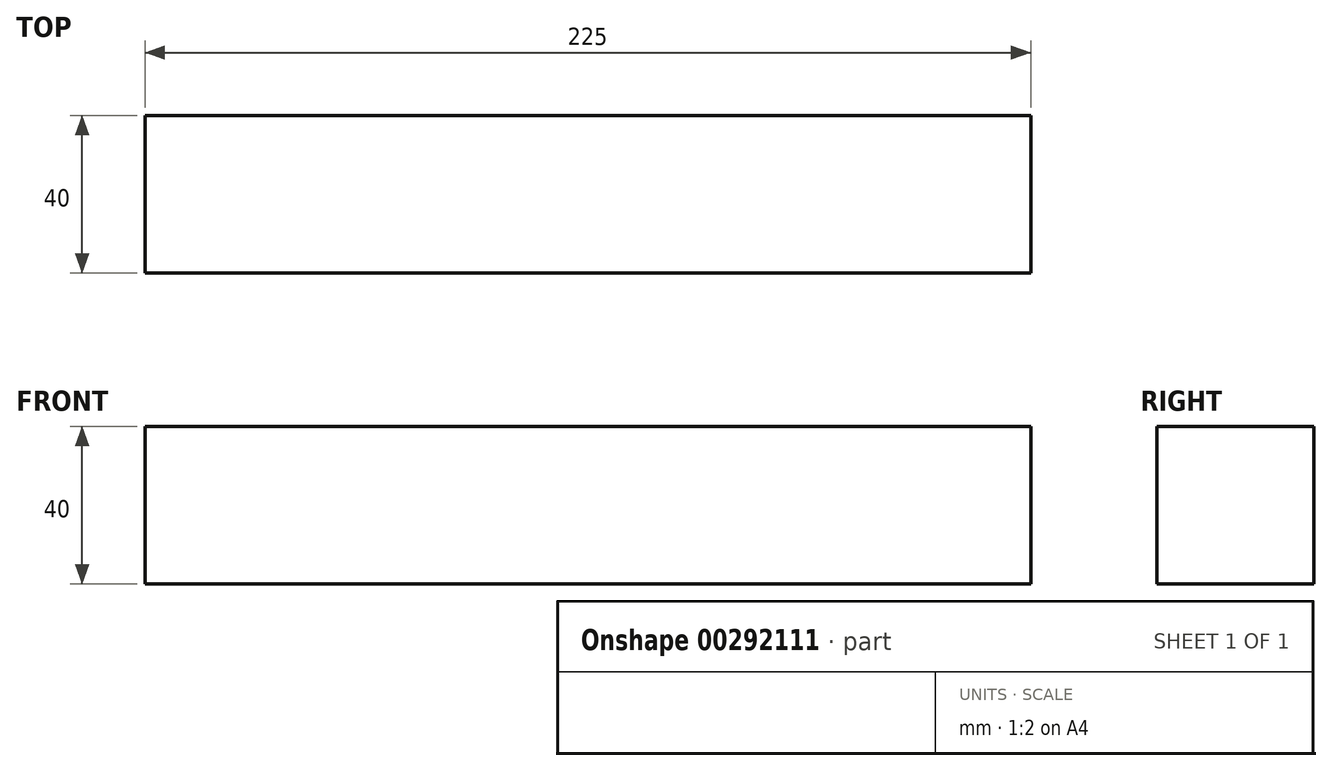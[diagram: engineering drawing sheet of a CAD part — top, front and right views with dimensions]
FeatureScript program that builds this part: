
annotation { "Feature Type Name" : "Feature", "Feature Type Description" : "" }
export const myFeature = defineFeature(function(context is Context, id is Id, definition is map)
    precondition{}
    {
        {
            var Q0;
            Q0=qCreatedBy(makeId("Front.planeOp"),FACE);
            var sketch = newSketch(context, id + "F0", { "sketchPlane" : qUnion([Q0])});
            skLineSegment(sketch, "E0.bottom", {"start": v(0, 0) * mm, "end": v(225, 0) * mm});
            skLineSegment(sketch, "E0.top", {"start": v(0, 40) * mm, "end": v(225, 40) * mm});
            skLineSegment(sketch, "E0.left", {"start": v(0, 0) * mm, "end": v(0, 40) * mm});
            skLineSegment(sketch, "E0.right", {"start": v(225, 0) * mm, "end": v(225, 40) * mm});
            skSolve(sketch);
        }
        {
            var Q0;
            Q0 = qSketchRegion(id + "F0", true);
            extrude(context, id + "F1", {"entities" : qUnion([Q0]), "depth" : 40 * mm});
        }
    });
